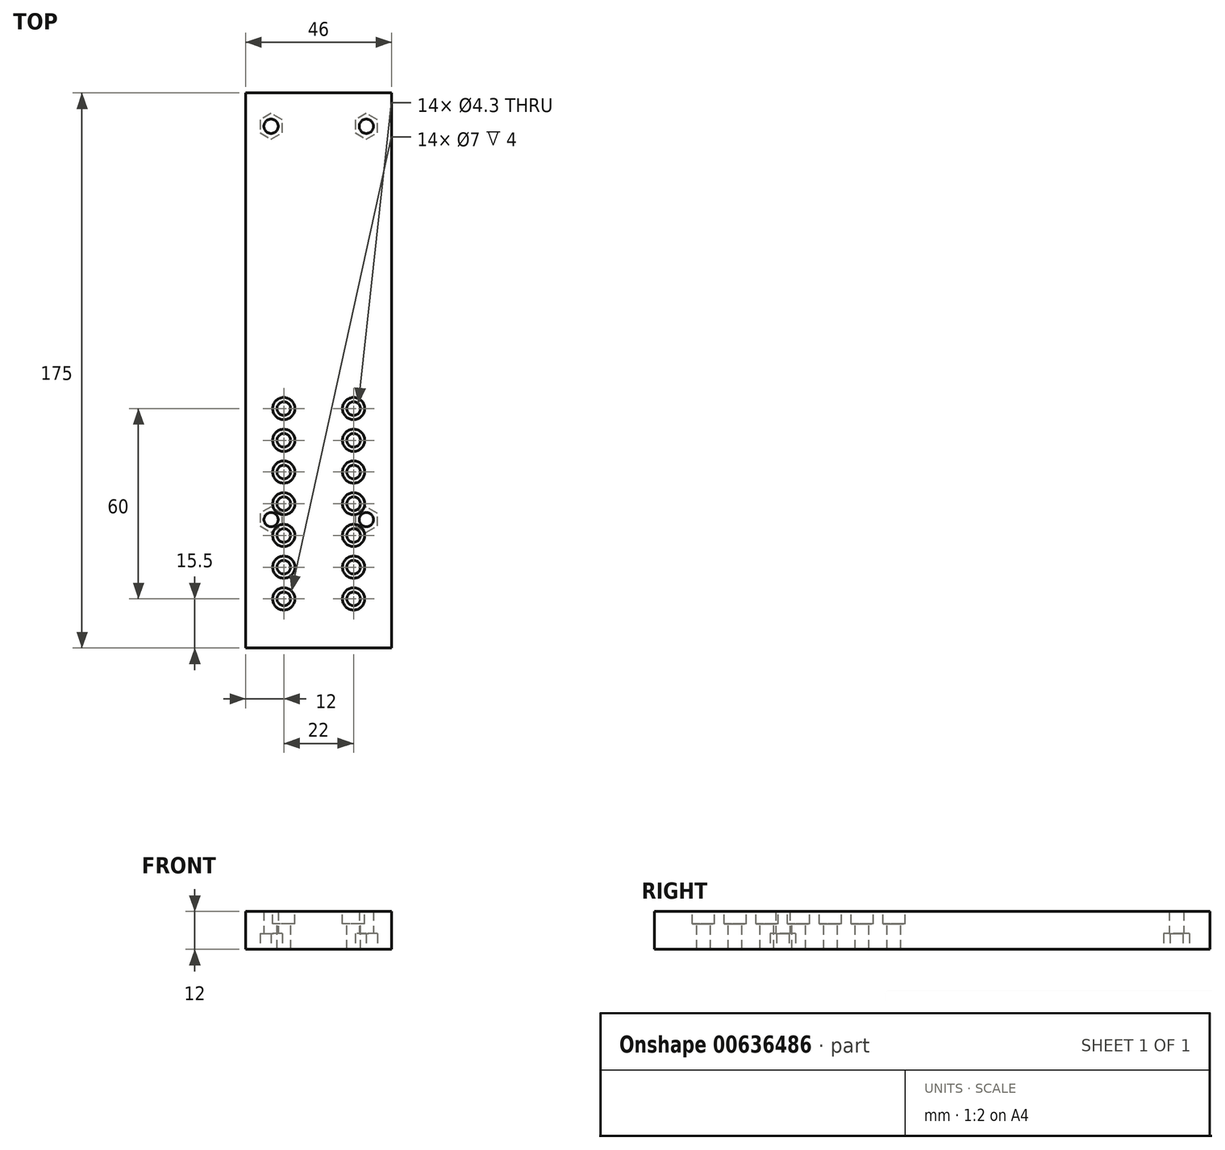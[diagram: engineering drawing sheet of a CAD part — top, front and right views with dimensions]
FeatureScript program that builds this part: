
annotation { "Feature Type Name" : "Feature", "Feature Type Description" : "" }
export const myFeature = defineFeature(function(context is Context, id is Id, definition is map)
    precondition{}
    {
        {
            var Q0;
            Q0=qCreatedBy(makeId("Top.planeOp"),FACE);
            var sketch = newSketch(context, id + "F0", { "sketchPlane" : qUnion([Q0])});
            skLineSegment(sketch, "E0.bottom", {"start": v(23, 72.5) * mm, "end": v(-23, 72.5) * mm});
            skLineSegment(sketch, "E0.top", {"start": v(23, -72.5) * mm, "end": v(-23, -72.5) * mm});
            skLineSegment(sketch, "E0.left", {"start": v(23, 72.5) * mm, "end": v(23, -72.5) * mm});
            skLineSegment(sketch, "E0.right", {"start": v(-23, 72.5) * mm, "end": v(-23, -72.5) * mm});
            skPoint(sketch, "E0.middle", {"position": v(0, 0) * mm});
            skLineSegment(sketch, "E1", {"start": v(0, -72.5) * mm, "end": v(0, 72.5) * mm, "construction": true});
            skLineSegment(sketch, "E2", {"start": v(-23, 0) * mm, "end": v(23, 0) * mm, "construction": true});
            skLineSegment(sketch, "E3.0", {"start": v(15, -72.5) * mm, "end": v(15, 72.5) * mm, "construction": true});
            skLineSegment(sketch, "E4.0", {"start": v(-15, -72.5) * mm, "end": v(-15, 72.5) * mm, "construction": true});
            skLineSegment(sketch, "E5.0", {"start": v(-23, -62) * mm, "end": v(23, -62) * mm, "construction": true});
            skLineSegment(sketch, "E6.0", {"start": v(-23, 62) * mm, "end": v(23, 62) * mm, "construction": true});
            skCircle(sketch, "E7", {"center": v(-15, 62) * mm, "radius": 2.25 * mm});
            skCircle(sketch, "E8", {"center": v(15, 62) * mm, "radius": 2.25 * mm});
            skCircle(sketch, "E9", {"center": v(15, -62) * mm, "radius": 2.25 * mm});
            skCircle(sketch, "E10", {"center": v(-15, -62) * mm, "radius": 2.25 * mm});
            skLineSegment(sketch, "E11", {"start": v(-23, -72.5) * mm, "end": v(-23, -102.5) * mm});
            skLineSegment(sketch, "E12", {"start": v(-23, -102.5) * mm, "end": v(23, -102.5) * mm});
            skLineSegment(sketch, "E13", {"start": v(23, -102.5) * mm, "end": v(23, -72.5) * mm});
            skSolve(sketch);
        }
        {
            var Q0;
            Q0 = qSketchRegion(id + "F0", true);
            extrude(context, id + "F1", {"entities" : qUnion([Q0]), "depth" : 12 * mm, "offsetDistance" : 25 * mm});
        }
        {
            var Q0;
            Q0=makeQuery(id+"F1.opExtrude","CAP_FACE",FACE,{"disambiguationData":[OSD([sQuery(id+"F0.wireOp",EDGE,"E0.bottom"),sQuery(id+"F0.wireOp",EDGE,"E0.top"),sQuery(id+"F0.wireOp",EDGE,"E0.left"),sQuery(id+"F0.wireOp",EDGE,"E0.right"),sQuery(id+"F0.wireOp",EDGE,"E7"),sQuery(id+"F0.wireOp",EDGE,"E8"),sQuery(id+"F0.wireOp",EDGE,"E9"),sQuery(id+"F0.wireOp",EDGE,"E10")])],"isStart":true});
            var sketch = newSketch(context, id + "F2", { "sketchPlane" : qUnion([Q0])});
            skCircle(sketch, "E14.cCircle", {"center": v(15, -62) * mm, "radius": 3.5 * mm, "construction": true});
            skLineSegment(sketch, "E14.0", {"start": v(11.5, -64.02) * mm, "end": v(11.5, -59.98) * mm});
            skLineSegment(sketch, "E14.1", {"start": v(11.5, -59.98) * mm, "end": v(15, -57.96) * mm});
            skLineSegment(sketch, "E14.2", {"start": v(15, -57.96) * mm, "end": v(18.5, -59.98) * mm});
            skLineSegment(sketch, "E14.3", {"start": v(18.5, -59.98) * mm, "end": v(18.5, -64.02) * mm});
            skLineSegment(sketch, "E14.4", {"start": v(18.5, -64.02) * mm, "end": v(15, -66.04) * mm});
            skLineSegment(sketch, "E14.5", {"start": v(15, -66.04) * mm, "end": v(11.5, -64.02) * mm});
            skPoint(sketch, "E14.0.midPoint", {"position": v(11.5, -62) * mm});
            skPoint(sketch, "E15.0.1.0", {"position": v(11.5, 62) * mm});
            skCircle(sketch, "E15.0.1.1", {"center": v(15, 62) * mm, "radius": 3.5 * mm, "construction": true});
            skLineSegment(sketch, "E15.0.1.2", {"start": v(18.5, 64.02) * mm, "end": v(18.5, 59.98) * mm});
            skLineSegment(sketch, "E15.0.1.3", {"start": v(11.5, 59.98) * mm, "end": v(11.5, 64.02) * mm});
            skLineSegment(sketch, "E15.0.1.4", {"start": v(11.5, 64.02) * mm, "end": v(15, 66.04) * mm});
            skLineSegment(sketch, "E15.0.1.5", {"start": v(15, 66.04) * mm, "end": v(18.5, 64.02) * mm});
            skLineSegment(sketch, "E15.0.1.6", {"start": v(18.5, 59.98) * mm, "end": v(15, 57.96) * mm});
            skLineSegment(sketch, "E15.0.1.7", {"start": v(15, 57.96) * mm, "end": v(11.5, 59.98) * mm});
            skPoint(sketch, "E15.1.0.0", {"position": v(-18.5, -62) * mm});
            skCircle(sketch, "E15.1.0.1", {"center": v(-15, -62) * mm, "radius": 3.5 * mm, "construction": true});
            skLineSegment(sketch, "E15.1.0.2", {"start": v(-11.5, -59.98) * mm, "end": v(-11.5, -64.02) * mm});
            skLineSegment(sketch, "E15.1.0.3", {"start": v(-18.5, -64.02) * mm, "end": v(-18.5, -59.98) * mm});
            skLineSegment(sketch, "E15.1.0.4", {"start": v(-18.5, -59.98) * mm, "end": v(-15, -57.96) * mm});
            skLineSegment(sketch, "E15.1.0.5", {"start": v(-15, -57.96) * mm, "end": v(-11.5, -59.98) * mm});
            skLineSegment(sketch, "E15.1.0.6", {"start": v(-11.5, -64.02) * mm, "end": v(-15, -66.04) * mm});
            skLineSegment(sketch, "E15.1.0.7", {"start": v(-15, -66.04) * mm, "end": v(-18.5, -64.02) * mm});
            skPoint(sketch, "E15.1.1.0", {"position": v(-18.5, 62) * mm});
            skCircle(sketch, "E15.1.1.1", {"center": v(-15, 62) * mm, "radius": 3.5 * mm, "construction": true});
            skLineSegment(sketch, "E15.1.1.2", {"start": v(-11.5, 64.02) * mm, "end": v(-11.5, 59.98) * mm});
            skLineSegment(sketch, "E15.1.1.3", {"start": v(-18.5, 59.98) * mm, "end": v(-18.5, 64.02) * mm});
            skLineSegment(sketch, "E15.1.1.4", {"start": v(-18.5, 64.02) * mm, "end": v(-15, 66.04) * mm});
            skLineSegment(sketch, "E15.1.1.5", {"start": v(-15, 66.04) * mm, "end": v(-11.5, 64.02) * mm});
            skLineSegment(sketch, "E15.1.1.6", {"start": v(-11.5, 59.98) * mm, "end": v(-15, 57.96) * mm});
            skLineSegment(sketch, "E15.1.1.7", {"start": v(-15, 57.96) * mm, "end": v(-18.5, 59.98) * mm});
            skLineSegment(sketch, "E15.direction1", {"start": v(11.5, -64.02) * mm, "end": v(-18.5, -64.02) * mm, "construction": true});
            skLineSegment(sketch, "E15.direction2", {"start": v(11.5, -64.02) * mm, "end": v(11.5, 59.98) * mm, "construction": true});
            skSolve(sketch);
        }
        {
            var Q0;
            Q0 = qSketchRegion(id + "F2", true);
            extrude(context, id + "F3", {"entities" : qUnion([Q0]), "operationType" : NewBodyOperationType.REMOVE, "oppositeDirection" : true, "depth" : 5 * mm, "offsetDistance" : 25 * mm});
        }
        {
            var Q0;
            Q0=makeQuery(id+"F1.opExtrude","CAP_FACE",FACE,{"disambiguationData":[OSD([sQuery(id+"F0.wireOp",EDGE,"E0.bottom"),sQuery(id+"F0.wireOp",EDGE,"E0.top"),sQuery(id+"F0.wireOp",EDGE,"E0.left"),sQuery(id+"F0.wireOp",EDGE,"E0.right"),sQuery(id+"F0.wireOp",EDGE,"E7"),sQuery(id+"F0.wireOp",EDGE,"E8"),sQuery(id+"F0.wireOp",EDGE,"E9"),sQuery(id+"F0.wireOp",EDGE,"E10")])],"isStart":false});
            var sketch = newSketch(context, id + "F4", { "sketchPlane" : qUnion([Q0])});
            skLineSegment(sketch, "E16", {"start": v(0, 72.5) * mm, "end": v(0, -72.5) * mm, "construction": true});
            skCircle(sketch, "E17", {"center": v(11, -67) * mm, "radius": 2.15 * mm});
            skCircle(sketch, "E18.0.1.0", {"center": v(11, -57) * mm, "radius": 2.15 * mm});
            skCircle(sketch, "E18.0.2.0", {"center": v(11, -47) * mm, "radius": 2.15 * mm});
            skCircle(sketch, "E18.0.3.0", {"center": v(11, -37) * mm, "radius": 2.15 * mm});
            skCircle(sketch, "E18.1.0.0", {"center": v(-11, -67) * mm, "radius": 2.15 * mm});
            skCircle(sketch, "E18.1.1.0", {"center": v(-11, -57) * mm, "radius": 2.15 * mm});
            skCircle(sketch, "E18.1.2.0", {"center": v(-11, -47) * mm, "radius": 2.15 * mm});
            skCircle(sketch, "E18.1.3.0", {"center": v(-11, -37) * mm, "radius": 2.15 * mm});
            skLineSegment(sketch, "E18.direction1", {"start": v(11, -67) * mm, "end": v(-11, -67) * mm, "construction": true});
            skLineSegment(sketch, "E18.direction2", {"start": v(11, -67) * mm, "end": v(11, -57) * mm, "construction": true});
            skCircle(sketch, "E19.0.0.4", {"center": v(11, -27) * mm, "radius": 2.15 * mm});
            skCircle(sketch, "E19.0.1.4", {"center": v(-11, -27) * mm, "radius": 2.15 * mm});
            skCircle(sketch, "E20", {"center": v(11, -77) * mm, "radius": 2.15 * mm});
            skCircle(sketch, "E21.0.1.0", {"center": v(11, -87) * mm, "radius": 2.15 * mm});
            skCircle(sketch, "E21.1.0.0", {"center": v(-11, -77) * mm, "radius": 2.15 * mm});
            skCircle(sketch, "E21.1.1.0", {"center": v(-11, -87) * mm, "radius": 2.15 * mm});
            skLineSegment(sketch, "E21.direction1", {"start": v(11, -77) * mm, "end": v(-11, -77) * mm, "construction": true});
            skLineSegment(sketch, "E21.direction2", {"start": v(11, -77) * mm, "end": v(11, -87) * mm, "construction": true});
            skSolve(sketch);
        }
        {
            var Q0;
            Q0 = qSketchRegion(id + "F4", true);
            extrude(context, id + "F5", {"entities" : qUnion([Q0]), "operationType" : NewBodyOperationType.REMOVE, "oppositeDirection" : true, "depth" : 25 * mm, "offsetDistance" : 25 * mm});
        }
        {
            var Q0;
            Q0=makeQuery(id+"F1.opExtrude","CAP_FACE",FACE,{"disambiguationData":[OSD([sQuery(id+"F0.wireOp",EDGE,"E0.bottom"),sQuery(id+"F0.wireOp",EDGE,"E0.top"),sQuery(id+"F0.wireOp",EDGE,"E0.left"),sQuery(id+"F0.wireOp",EDGE,"E0.right"),sQuery(id+"F0.wireOp",EDGE,"E7"),sQuery(id+"F0.wireOp",EDGE,"E8"),sQuery(id+"F0.wireOp",EDGE,"E9"),sQuery(id+"F0.wireOp",EDGE,"E10")])],"isStart":false});
            var sketch = newSketch(context, id + "F6", { "sketchPlane" : qUnion([Q0])});
            skCircle(sketch, "E22", {"center": v(11, -67) * mm, "radius": 3.5 * mm});
            skCircle(sketch, "E23.0.1.0", {"center": v(11, -57) * mm, "radius": 3.5 * mm});
            skCircle(sketch, "E23.0.2.0", {"center": v(11, -47) * mm, "radius": 3.5 * mm});
            skCircle(sketch, "E23.0.3.0", {"center": v(11, -37) * mm, "radius": 3.5 * mm});
            skCircle(sketch, "E23.0.4.0", {"center": v(11, -27) * mm, "radius": 3.5 * mm});
            skCircle(sketch, "E23.1.0.0", {"center": v(-11, -67) * mm, "radius": 3.5 * mm});
            skCircle(sketch, "E23.1.1.0", {"center": v(-11, -57) * mm, "radius": 3.5 * mm});
            skCircle(sketch, "E23.1.2.0", {"center": v(-11, -47) * mm, "radius": 3.5 * mm});
            skCircle(sketch, "E23.1.3.0", {"center": v(-11, -37) * mm, "radius": 3.5 * mm});
            skCircle(sketch, "E23.1.4.0", {"center": v(-11, -27) * mm, "radius": 3.5 * mm});
            skLineSegment(sketch, "E23.direction1", {"start": v(11, -67) * mm, "end": v(-11, -67) * mm, "construction": true});
            skLineSegment(sketch, "E23.direction2", {"start": v(11, -67) * mm, "end": v(11, -57) * mm, "construction": true});
            skSolve(sketch);
        }
        {
            var Q0;
            Q0 = qSketchRegion(id + "F6", true);
            extrude(context, id + "F7", {"entities" : qUnion([Q0]), "operationType" : NewBodyOperationType.REMOVE, "oppositeDirection" : true, "depth" : 4 * mm, "offsetDistance" : 25 * mm});
        }
        {
            var Q0;
            Q0=makeQuery(id+"F1.opExtrude","CAP_FACE",FACE,{"disambiguationData":[OSD([sQuery(id+"F0.wireOp",EDGE,"E0.bottom"),sQuery(id+"F0.wireOp",EDGE,"E0.left"),sQuery(id+"F0.wireOp",EDGE,"E0.right"),sQuery(id+"F0.wireOp",EDGE,"E7"),sQuery(id+"F0.wireOp",EDGE,"E8"),sQuery(id+"F0.wireOp",EDGE,"E9"),sQuery(id+"F0.wireOp",EDGE,"E10"),sQuery(id+"F0.wireOp",EDGE,"E11"),sQuery(id+"F0.wireOp",EDGE,"E12"),sQuery(id+"F0.wireOp",EDGE,"E13")])],"isStart":false});
            var sketch = newSketch(context, id + "F8", { "sketchPlane" : qUnion([Q0])});
            skCircle(sketch, "E24", {"center": v(-11, -77) * mm, "radius": 3.5 * mm});
            skCircle(sketch, "E25.0.1.0", {"center": v(-11, -87) * mm, "radius": 3.5 * mm});
            skCircle(sketch, "E25.1.0.0", {"center": v(11, -77) * mm, "radius": 3.5 * mm});
            skCircle(sketch, "E25.1.1.0", {"center": v(11, -87) * mm, "radius": 3.5 * mm});
            skLineSegment(sketch, "E25.direction1", {"start": v(-11, -77) * mm, "end": v(11, -77) * mm, "construction": true});
            skLineSegment(sketch, "E25.direction2", {"start": v(-11, -77) * mm, "end": v(-11, -87) * mm, "construction": true});
            skSolve(sketch);
        }
        {
            var Q0;
            Q0 = qSketchRegion(id + "F8", true);
            extrude(context, id + "F9", {"entities" : qUnion([Q0]), "operationType" : NewBodyOperationType.REMOVE, "oppositeDirection" : true, "depth" : 4 * mm, "offsetDistance" : 25 * mm});
        }
    });
